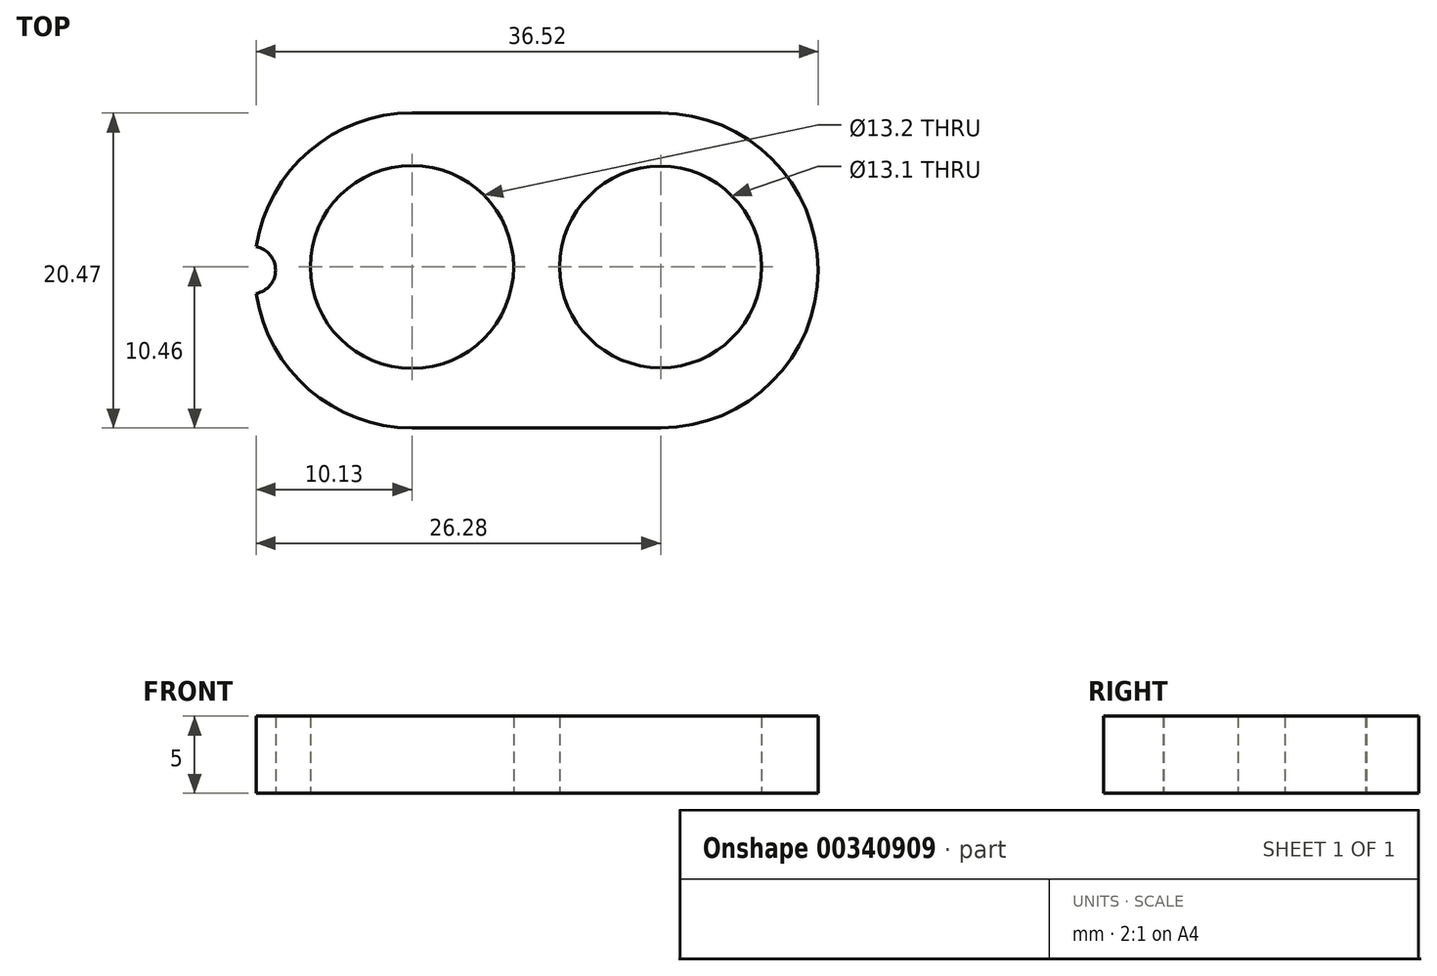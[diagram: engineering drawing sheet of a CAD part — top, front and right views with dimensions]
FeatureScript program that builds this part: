
annotation { "Feature Type Name" : "Feature", "Feature Type Description" : "" }
export const myFeature = defineFeature(function(context is Context, id is Id, definition is map)
    precondition{}
    {
        {
            var Q0;
            Q0=qCreatedBy(makeId("Top.planeOp"),FACE);
            var sketch = newSketch(context, id + "F0", { "sketchPlane" : qUnion([Q0])});
            skCircle(sketch, "E0", {"center": v(0, 0) * mm, "radius": 6.6 * mm});
            skCircle(sketch, "E1", {"center": v(16.15, 0) * mm, "radius": 6.55 * mm});
            skLineSegment(sketch, "E2", {"start": v(0, 10.01) * mm, "end": v(16.15, 10.01) * mm});
            skLineSegment(sketch, "E3", {"start": v(0, -10.46) * mm, "end": v(16.15, -10.46) * mm});
            skArc(sketch, "E4", {"start": v(0, 10.01) * mm, "mid": v(-6.67, 7.54) * mm, "end": v(-10.12, 1.31) * mm});
            skArc(sketch, "E5", {"start": v(16.15, -10.46) * mm, "mid": v(26.39, -0.22) * mm, "end": v(16.15, 10.01) * mm});
            skArc(sketch, "E6", {"start": v(-10.13, -1.72) * mm, "mid": v(-8.87, -0.2) * mm, "end": v(-10.12, 1.31) * mm});
            skArc(sketch, "E7.trimOffspring", {"start": v(-10.13, -1.72) * mm, "mid": v(-6.69, -7.97) * mm, "end": v(0, -10.46) * mm});
            skSolve(sketch);
        }
        {
            var Q0;
            Q0 = qSketchRegion(id + "F0", true);
            extrude(context, id + "F1", {"entities" : qUnion([Q0]), "depth" : 5 * mm, "offsetDistance" : 25 * mm});
        }
    });
